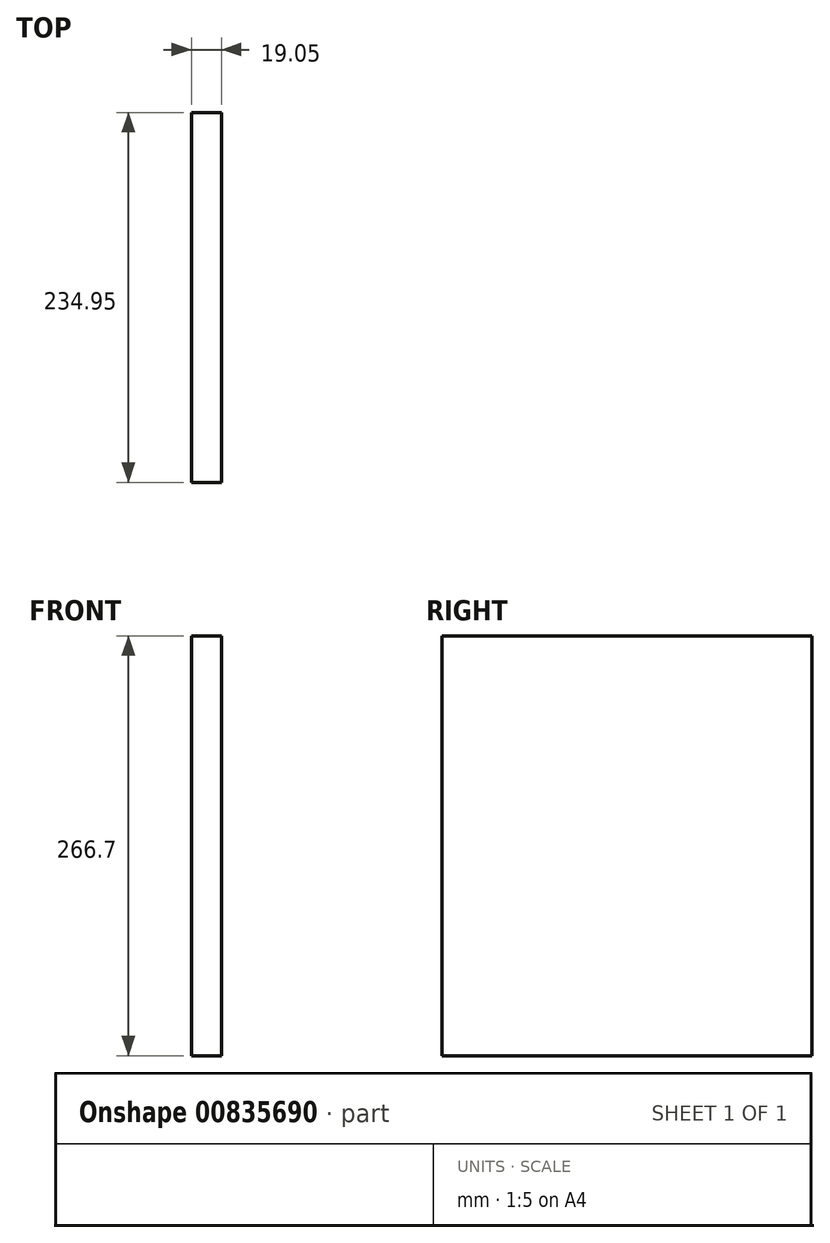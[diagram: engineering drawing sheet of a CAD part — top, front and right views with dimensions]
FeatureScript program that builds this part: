
annotation { "Feature Type Name" : "Feature", "Feature Type Description" : "" }
export const myFeature = defineFeature(function(context is Context, id is Id, definition is map)
    precondition{}
    {
        {
            var Q0;
            Q0=qCreatedBy(makeId("Right.planeOp"),FACE);
            var sketch = newSketch(context, id + "F0", { "sketchPlane" : qUnion([Q0])});
            skLineSegment(sketch, "E0.bottom", {"start": v(0, 0) * mm, "end": v(234.95, 0) * mm});
            skLineSegment(sketch, "E0.top", {"start": v(0, 266.7) * mm, "end": v(234.95, 266.7) * mm});
            skLineSegment(sketch, "E0.left", {"start": v(0, 0) * mm, "end": v(0, 266.7) * mm});
            skLineSegment(sketch, "E0.right", {"start": v(234.95, 0) * mm, "end": v(234.95, 266.7) * mm});
            skSolve(sketch);
        }
        {
            var Q0;
            Q0=qSketchRegion(id+"F0",true);
            extrude(context, id + "F1", {"entities" : qUnion([Q0]), "depth" : 19.05 * mm, "offsetDistance" : 25.4 * mm});
        }
    });
